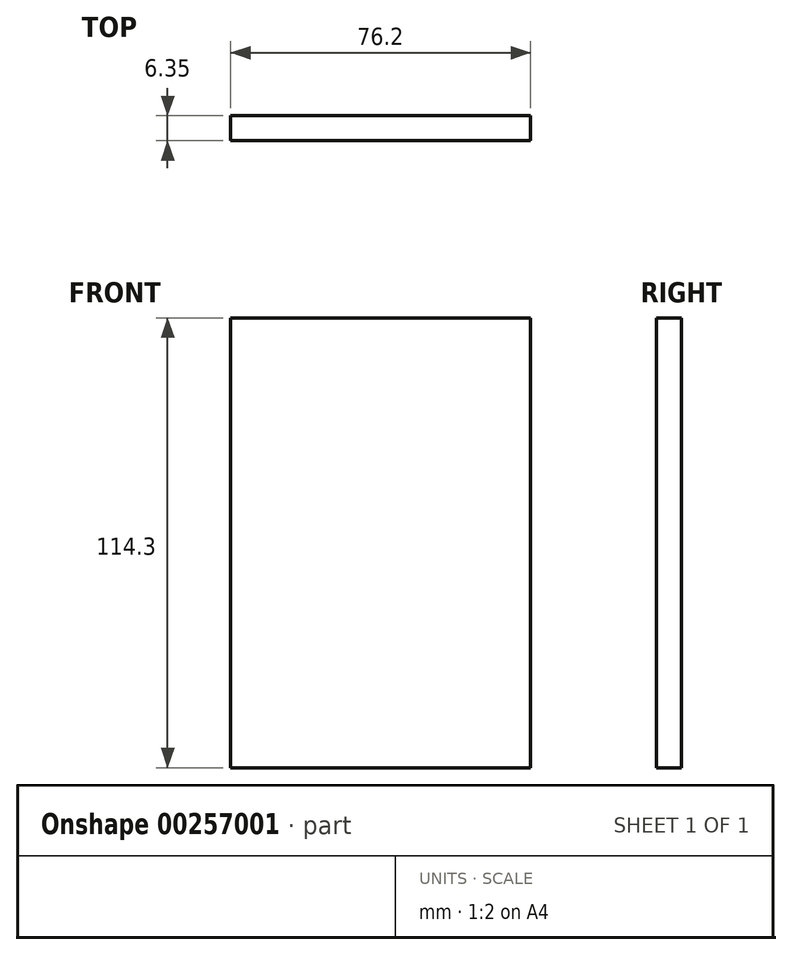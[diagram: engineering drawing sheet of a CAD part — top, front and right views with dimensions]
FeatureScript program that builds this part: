
annotation { "Feature Type Name" : "Feature", "Feature Type Description" : "" }
export const myFeature = defineFeature(function(context is Context, id is Id, definition is map)
    precondition{}
    {
        {
            var Q0;
            Q0=qCreatedBy(makeId("Front.planeOp"),FACE);
            var sketch = newSketch(context, id + "F0", { "sketchPlane" : qUnion([Q0])});
            skLineSegment(sketch, "E0.bottom", {"start": v(-76.2, 8.65) * mm, "end": v(0, 8.65) * mm});
            skLineSegment(sketch, "E0.top", {"start": v(-76.2, -105.65) * mm, "end": v(0, -105.65) * mm});
            skLineSegment(sketch, "E0.left", {"start": v(-76.2, 8.65) * mm, "end": v(-76.2, -105.65) * mm});
            skLineSegment(sketch, "E0.right", {"start": v(0, 8.65) * mm, "end": v(0, -105.65) * mm});
            skSolve(sketch);
        }
        {
            var Q0;
            Q0=makeQuery(id+"F0.imprint","IMPRINT",FACE,{"disambiguationData":[TD([[makeQuery(id+"F0.imprint","IMPRINT",EDGE,{"derivedFrom":sQuery(id+"F0.wireOp",EDGE,"E0.bottom")}),-1.0]])]});
            extrude(context, id + "F1", {"entities" : qUnion([Q0]), "depth" : 6.35 * mm});
        }
    });
